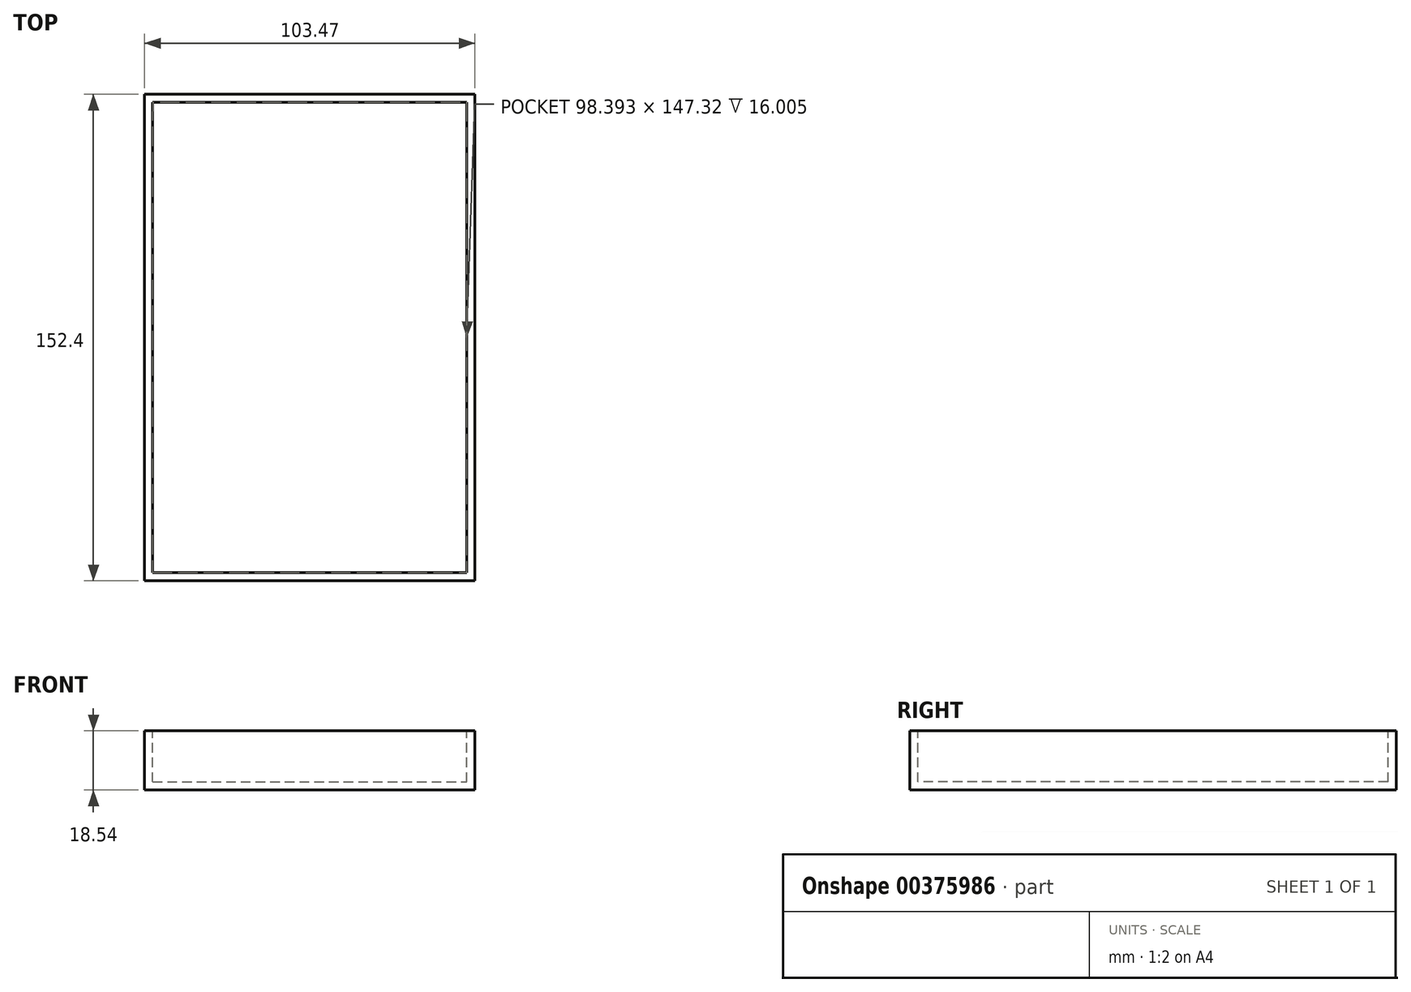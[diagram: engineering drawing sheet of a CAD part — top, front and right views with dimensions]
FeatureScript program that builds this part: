
annotation { "Feature Type Name" : "Feature", "Feature Type Description" : "" }
export const myFeature = defineFeature(function(context is Context, id is Id, definition is map)
    precondition{}
    {
        {
            var Q0;
            Q0=qCreatedBy(makeId("Front.planeOp"),FACE);
            var sketch = newSketch(context, id + "F0", { "sketchPlane" : qUnion([Q0])});
            skLineSegment(sketch, "E0.bottom", {"start": v(0, 0) * mm, "end": v(103.47, 0) * mm});
            skLineSegment(sketch, "E0.top", {"start": v(0, 18.54) * mm, "end": v(103.47, 18.54) * mm});
            skLineSegment(sketch, "E0.left", {"start": v(0, 0) * mm, "end": v(0, 18.54) * mm});
            skLineSegment(sketch, "E0.right", {"start": v(103.47, 0) * mm, "end": v(103.47, 18.54) * mm});
            skSolve(sketch);
        }
        {
            var Q0;
            Q0 = qSketchRegion(id + "F0", true);
            extrude(context, id + "F1", {"entities" : qUnion([Q0]), "endBound" : BoundingType.SYMMETRIC, "oppositeDirection" : true, "depth" : 152.4 * mm});
        }
        {
            var Q0;
            Q0=makeQuery(id+"F1.opExtrude","SWEPT_FACE",FACE,{"disambiguationData":[OSD([sQuery(id+"F0.wireOp",EDGE,"E0.top")])]});
            shell(context, id + "F2", {"entities" : qUnion([Q0]), "thickness" : 2.54 * mm});
        }
    });
